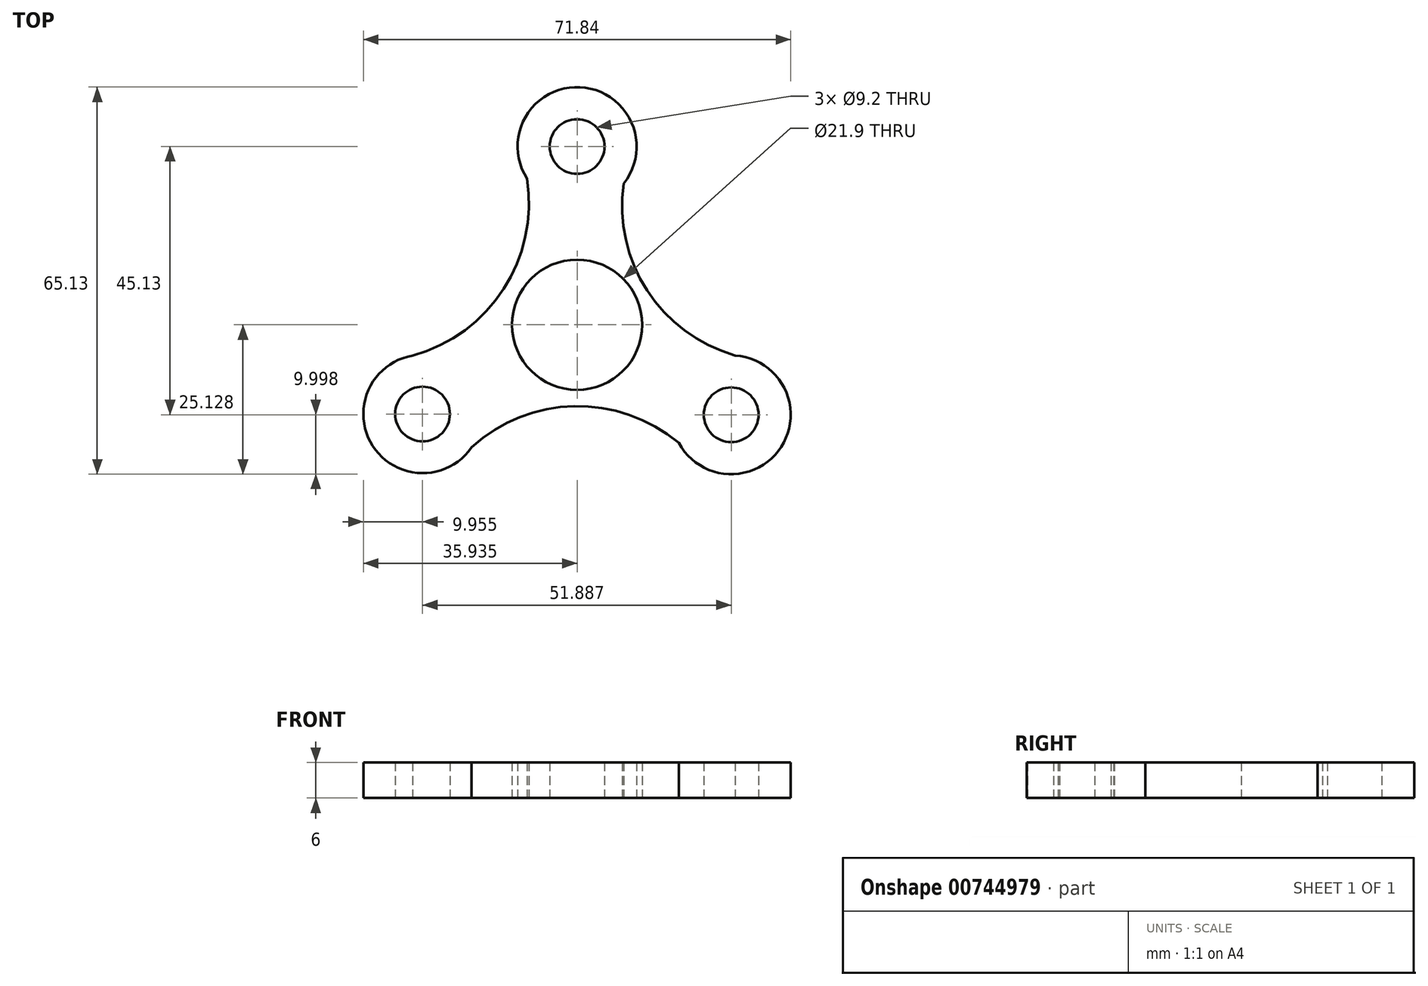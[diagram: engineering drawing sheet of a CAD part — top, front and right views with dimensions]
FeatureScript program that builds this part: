
annotation { "Feature Type Name" : "Feature", "Feature Type Description" : "" }
export const myFeature = defineFeature(function(context is Context, id is Id, definition is map)
    precondition{}
    {
        {
            var Q0;
            Q0=qCreatedBy(makeId("Top.planeOp"),FACE);
            var sketch = newSketch(context, id + "F0", { "sketchPlane" : qUnion([Q0])});
            skCircle(sketch, "E0", {"center": v(-80.93, -11.97) * mm, "radius": 10.95 * mm});
            skCircle(sketch, "E1", {"center": v(-55.03, -27.1) * mm, "radius": 4.6 * mm});
            skCircle(sketch, "E2", {"center": v(-106.92, -26.97) * mm, "radius": 4.6 * mm});
            skCircle(sketch, "E3", {"center": v(-80.93, 18.03) * mm, "radius": 4.6 * mm});
            skArc(sketch, "E4", {"start": v(-73.1, 11.82) * mm, "mid": v(-80.44, 28.02) * mm, "end": v(-89.35, 12.62) * mm});
            skArc(sketch, "E5", {"start": v(-63.83, -31.85) * mm, "mid": v(-46.62, -32.52) * mm, "end": v(-54.34, -17.13) * mm});
            skArc(sketch, "E6", {"start": v(-108.6, -17.16) * mm, "mid": v(-115.3, -32.35) * mm, "end": v(-98.7, -32.6) * mm});
            skArc(sketch, "E7", {"start": v(-108.6, -17.16) * mm, "mid": v(-93.3, -5.94) * mm, "end": v(-89.35, 12.62) * mm});
            skArc(sketch, "E8", {"start": v(-73.1, 11.82) * mm, "mid": v(-69.17, -6.19) * mm, "end": v(-54.34, -17.13) * mm});
            skArc(sketch, "E9", {"start": v(-63.83, -31.85) * mm, "mid": v(-81.4, -25.67) * mm, "end": v(-98.7, -32.6) * mm});
            skSolve(sketch);
        }
        {
            var Q0;
            Q0 = qSketchRegion(id + "F0", true);
            extrude(context, id + "F1", {"entities" : qUnion([Q0]), "depth" : 6 * mm, "offsetDistance" : 25 * mm});
        }
    });
